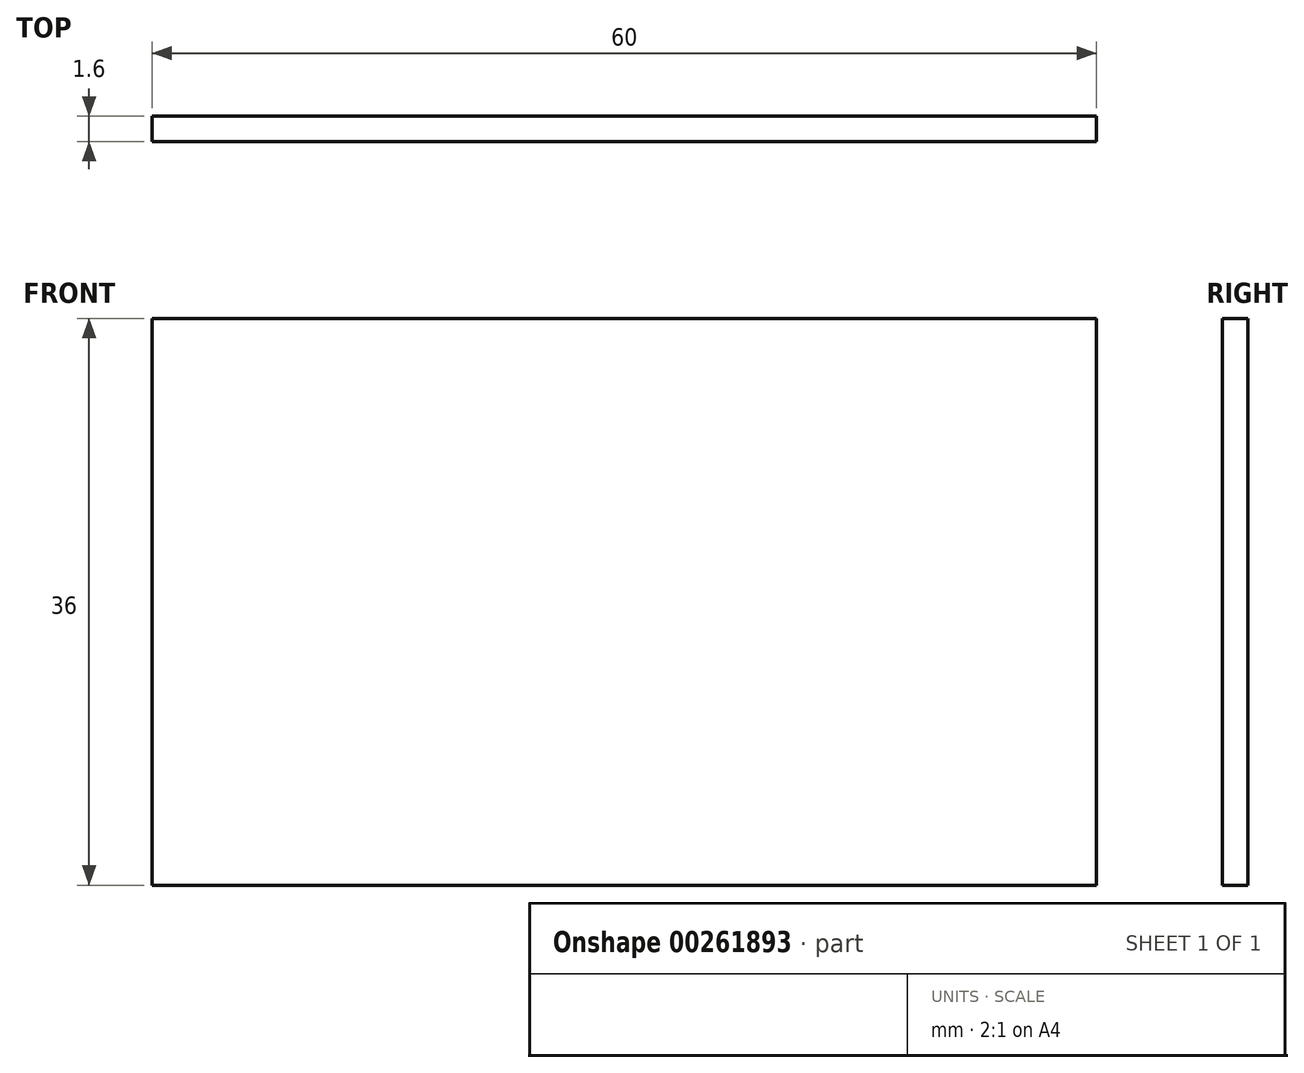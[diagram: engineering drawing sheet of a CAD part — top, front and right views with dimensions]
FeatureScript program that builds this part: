
annotation { "Feature Type Name" : "Feature", "Feature Type Description" : "" }
export const myFeature = defineFeature(function(context is Context, id is Id, definition is map)
    precondition{}
    {
        {
            var Q0;
            Q0=qCreatedBy(makeId("Front.planeOp"),FACE);
            var sketch = newSketch(context, id + "F0", { "sketchPlane" : qUnion([Q0])});
            skLineSegment(sketch, "E0.bottom", {"start": v(0, 0) * mm, "end": v(-60, 0) * mm});
            skLineSegment(sketch, "E0.top", {"start": v(0, 36) * mm, "end": v(-60, 36) * mm});
            skLineSegment(sketch, "E0.left", {"start": v(0, 0) * mm, "end": v(0, 36) * mm});
            skLineSegment(sketch, "E0.right", {"start": v(-60, 0) * mm, "end": v(-60, 36) * mm});
            skSolve(sketch);
        }
        {
            var Q0;
            Q0=makeQuery(id+"F0.imprint","IMPRINT",FACE,{"disambiguationData":[TD([[makeQuery(id+"F0.imprint","IMPRINT",EDGE,{"derivedFrom":sQuery(id+"F0.wireOp",EDGE,"E0.bottom")}),-1.0]])]});
            extrude(context, id + "F1", {"entities" : qUnion([Q0]), "depth" : 1.6 * mm});
        }
    });
